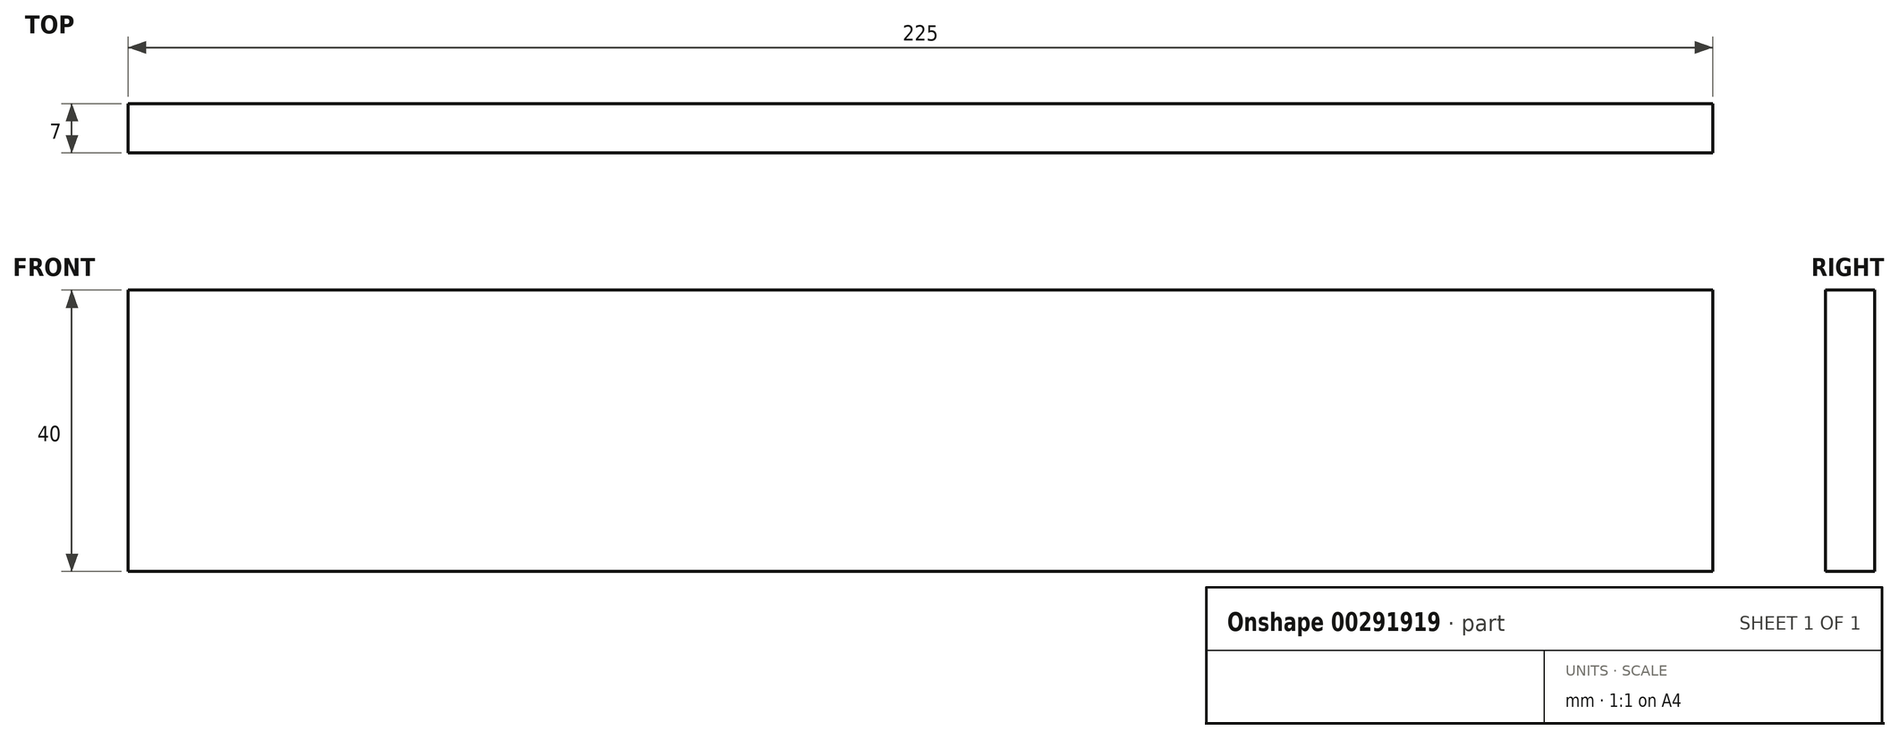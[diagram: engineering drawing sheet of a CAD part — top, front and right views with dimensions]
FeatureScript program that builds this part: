
annotation { "Feature Type Name" : "Feature", "Feature Type Description" : "" }
export const myFeature = defineFeature(function(context is Context, id is Id, definition is map)
    precondition{}
    {
        {
            var Q0;
            Q0=qCreatedBy(makeId("Front.planeOp"),FACE);
            var sketch = newSketch(context, id + "F0", { "sketchPlane" : qUnion([Q0])});
            skLineSegment(sketch, "E0", {"start": v(0, 20) * mm, "end": v(112.5, 20) * mm});
            skLineSegment(sketch, "E1", {"start": v(112.5, 20) * mm, "end": v(112.5, 0) * mm});
            skLineSegment(sketch, "E2.MirrorCS", {"start": v(0, -20) * mm, "end": v(112.5, -20) * mm});
            skLineSegment(sketch, "E3.MirrorCS", {"start": v(112.5, -20) * mm, "end": v(112.5, 0) * mm});
            skLineSegment(sketch, "E4.MirrorCS", {"start": v(0, 20) * mm, "end": v(-112.5, 20) * mm});
            skLineSegment(sketch, "E5.MirrorCS", {"start": v(0, -20) * mm, "end": v(-112.5, -20) * mm});
            skLineSegment(sketch, "E6.MirrorCS", {"start": v(-112.5, 20) * mm, "end": v(-112.5, 0) * mm});
            skLineSegment(sketch, "E7.MirrorCS", {"start": v(-112.5, -20) * mm, "end": v(-112.5, 0) * mm});
            skSolve(sketch);
        }
        {
            var Q0;
            Q0=makeQuery(id+"F0.imprint","IMPRINT",FACE,{"disambiguationData":[TD([[makeQuery(id+"F0.imprint","IMPRINT",EDGE,{"derivedFrom":sQuery(id+"F0.wireOp",EDGE,"E0")}),-1.0]])]});
            extrude(context, id + "F1", {"entities" : qUnion([Q0]), "endBound" : BoundingType.SYMMETRIC, "depth" : 7 * mm});
        }
    });
